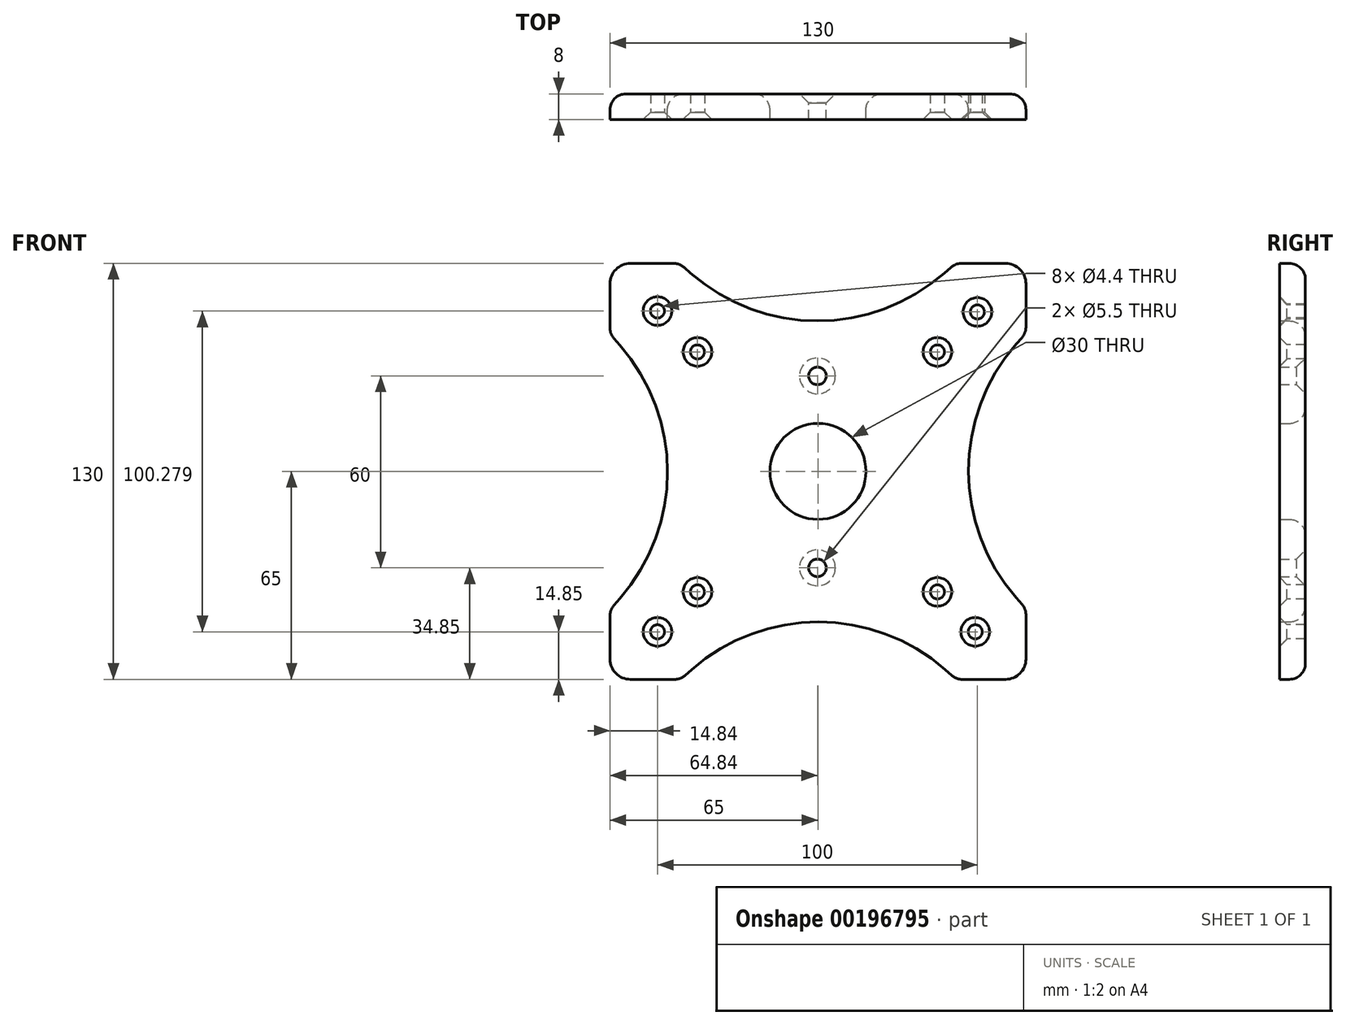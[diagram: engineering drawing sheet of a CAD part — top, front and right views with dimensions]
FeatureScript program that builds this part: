
annotation { "Feature Type Name" : "Feature", "Feature Type Description" : "" }
export const myFeature = defineFeature(function(context is Context, id is Id, definition is map)
    precondition{}
    {
        {
            var Q0;
            Q0=qCreatedBy(makeId("Front.planeOp"),FACE);
            var sketch = newSketch(context, id + "F0", { "sketchPlane" : qUnion([Q0])});
            skLineSegment(sketch, "E0.bottom", {"start": v(-58.49, 65.15) * mm, "end": v(-44.96, 65.15) * mm});
            skLineSegment(sketch, "E0.top", {"start": v(-58.49, -64.85) * mm, "end": v(-44.65, -64.85) * mm});
            skLineSegment(sketch, "E0.left", {"start": v(-64.84, 58.8) * mm, "end": v(-64.84, 44.96) * mm});
            skLineSegment(sketch, "E0.right", {"start": v(65.16, 58.8) * mm, "end": v(65.16, 45.27) * mm});
            skPoint(sketch, "E1.orphan", {"position": v(0, -0.9) * mm});
            skPoint(sketch, "E2.visualSharp", {"position": v(-64.84, 65.15) * mm});
            skArc(sketch, "E2.filletArc", {"start": v(-58.49, 65.15) * mm, "mid": v(-62.98, 63.3) * mm, "end": v(-64.84, 58.8) * mm});
            skPoint(sketch, "E3.visualSharp", {"position": v(65.16, 65.15) * mm});
            skArc(sketch, "E3.filletArc", {"start": v(65.16, 58.8) * mm, "mid": v(63.3, 63.3) * mm, "end": v(58.81, 65.15) * mm});
            skPoint(sketch, "E4.visualSharp", {"position": v(65.16, -64.85) * mm});
            skArc(sketch, "E4.filletArc", {"start": v(58.81, -64.85) * mm, "mid": v(63.3, -62.99) * mm, "end": v(65.16, -58.5) * mm});
            skPoint(sketch, "E5.visualSharp", {"position": v(-64.84, -64.85) * mm});
            skArc(sketch, "E5.filletArc", {"start": v(-64.84, -58.5) * mm, "mid": v(-62.98, -62.99) * mm, "end": v(-58.49, -64.85) * mm});
            skPoint(sketch, "E6", {"position": v(-106.96, 0) * mm});
            skArc(sketch, "E7", {"start": v(-61.82, -39.65) * mm, "mid": v(-46.88, 0) * mm, "end": v(-61.82, 39.65) * mm});
            skLineSegment(sketch, "E8.trimOffspring", {"start": v(-64.84, -44.96) * mm, "end": v(-64.84, -58.5) * mm});
            skLineSegment(sketch, "E9", {"start": v(-61.82, 39.65) * mm, "end": v(-63.6, 41.66) * mm});
            skLineSegment(sketch, "E10", {"start": v(-106.96, 0) * mm, "end": v(0, 0) * mm, "construction": true});
            skLineSegment(sketch, "E11.MirrorCS", {"start": v(-61.82, -39.65) * mm, "end": v(-63.6, -41.66) * mm});
            skLineSegment(sketch, "E12.1.0", {"start": v(39.96, -61.83) * mm, "end": v(41.98, -63.6) * mm});
            skArc(sketch, "E12.1.1", {"start": v(39.96, -61.83) * mm, "mid": v(0.31, -46.9) * mm, "end": v(-39.34, -61.83) * mm});
            skLineSegment(sketch, "E12.1.2", {"start": v(-39.34, -61.83) * mm, "end": v(-41.35, -63.6) * mm});
            skLineSegment(sketch, "E12.2.0", {"start": v(62.14, 39.95) * mm, "end": v(63.92, 41.97) * mm});
            skArc(sketch, "E12.2.1", {"start": v(62.14, 39.95) * mm, "mid": v(47.2, 0.3) * mm, "end": v(62.14, -39.35) * mm});
            skLineSegment(sketch, "E12.2.2", {"start": v(62.14, -39.35) * mm, "end": v(63.92, -41.36) * mm});
            skLineSegment(sketch, "E12.3.0", {"start": v(-39.64, 62.13) * mm, "end": v(-41.66, 63.9) * mm});
            skArc(sketch, "E12.3.1", {"start": v(-39.64, 62.13) * mm, "mid": v(0, 47.2) * mm, "end": v(39.66, 62.13) * mm});
            skLineSegment(sketch, "E12.3.2", {"start": v(39.66, 62.13) * mm, "end": v(41.67, 63.9) * mm});
            skPoint(sketch, "E12.center", {"position": v(0.16, 0.15) * mm});
            skLineSegment(sketch, "E13.trimOffspring", {"start": v(44.97, 65.15) * mm, "end": v(58.81, 65.15) * mm});
            skLineSegment(sketch, "E14.trimOffspring", {"start": v(65.16, -44.66) * mm, "end": v(65.16, -58.5) * mm});
            skLineSegment(sketch, "E15.trimOffspring", {"start": v(45.28, -64.85) * mm, "end": v(58.81, -64.85) * mm});
            skPoint(sketch, "E16.visualSharp", {"position": v(-64.84, 43.08) * mm});
            skArc(sketch, "E16.filletArc", {"start": v(-64.84, 44.96) * mm, "mid": v(-64.52, 43.2) * mm, "end": v(-63.6, 41.66) * mm});
            skPoint(sketch, "E17.visualSharp", {"position": v(-43.07, 65.15) * mm});
            skArc(sketch, "E17.filletArc", {"start": v(-41.66, 63.9) * mm, "mid": v(-43.2, 64.83) * mm, "end": v(-44.96, 65.15) * mm});
            skPoint(sketch, "E18.visualSharp", {"position": v(43.1, 65.15) * mm});
            skArc(sketch, "E18.filletArc", {"start": v(44.97, 65.15) * mm, "mid": v(43.21, 64.83) * mm, "end": v(41.67, 63.9) * mm});
            skPoint(sketch, "E19.visualSharp", {"position": v(65.16, 43.38) * mm});
            skArc(sketch, "E19.filletArc", {"start": v(63.92, 41.97) * mm, "mid": v(64.84, 43.5) * mm, "end": v(65.16, 45.27) * mm});
            skPoint(sketch, "E20.visualSharp", {"position": v(65.16, -42.78) * mm});
            skArc(sketch, "E20.filletArc", {"start": v(65.16, -44.66) * mm, "mid": v(64.84, -42.9) * mm, "end": v(63.92, -41.36) * mm});
            skPoint(sketch, "E21.visualSharp", {"position": v(43.4, -64.85) * mm});
            skArc(sketch, "E21.filletArc", {"start": v(41.98, -63.6) * mm, "mid": v(43.51, -64.53) * mm, "end": v(45.28, -64.85) * mm});
            skPoint(sketch, "E22.visualSharp", {"position": v(-42.77, -64.85) * mm});
            skArc(sketch, "E22.filletArc", {"start": v(-44.65, -64.85) * mm, "mid": v(-42.9, -64.53) * mm, "end": v(-41.35, -63.6) * mm});
            skPoint(sketch, "E23.visualSharp", {"position": v(-64.84, -43.08) * mm});
            skArc(sketch, "E23.filletArc", {"start": v(-63.6, -41.66) * mm, "mid": v(-64.52, -43.2) * mm, "end": v(-64.84, -44.96) * mm});
            skCircle(sketch, "E24", {"center": v(0.16, 0.15) * mm, "radius": 15 * mm});
            skSolve(sketch);
        }
        {
            var Q0;
            Q0=qSketchRegion(id+"F0",true);
            extrude(context, id + "F1", {"entities" : qUnion([Q0]), "depth" : 8 * mm});
        }
        {
            var Q0;
            Q0=makeQuery(id+"F1.opExtrude","CAP_FACE",FACE,{"disambiguationData":[OSD([sQuery(id+"F0.wireOp",EDGE,"E0.bottom"),sQuery(id+"F0.wireOp",EDGE,"E0.top"),sQuery(id+"F0.wireOp",EDGE,"E0.left"),sQuery(id+"F0.wireOp",EDGE,"E0.right"),sQuery(id+"F0.wireOp",EDGE,"E2.filletArc"),sQuery(id+"F0.wireOp",EDGE,"E3.filletArc"),sQuery(id+"F0.wireOp",EDGE,"E4.filletArc"),sQuery(id+"F0.wireOp",EDGE,"E5.filletArc")])],"isStart":false});
            var sketch = newSketch(context, id + "F2", { "sketchPlane" : qUnion([Q0])});
            skPoint(sketch, "E25", {"position": v(50, 50) * mm});
            skPoint(sketch, "E26", {"position": v(-50, 50.28) * mm});
            skPoint(sketch, "E27", {"position": v(-50, -50) * mm});
            skPoint(sketch, "E28", {"position": v(49.32, -50) * mm});
            skPoint(sketch, "E29", {"position": v(-37.5, 37.5) * mm});
            skPoint(sketch, "E30", {"position": v(-37.5, -37.5) * mm});
            skPoint(sketch, "E31", {"position": v(37.5, 37.5) * mm});
            skPoint(sketch, "E32", {"position": v(37.5, -37.5) * mm});
            skSolve(sketch);
        }
        {
            var Q0;
            Q0=sQuery(id+"F2.wireOp",VERTEX,"E26");
            var Q1;
            Q1=sQuery(id+"F2.wireOp",VERTEX,"E25");
            var Q2;
            Q2=sQuery(id+"F2.wireOp",VERTEX,"E28");
            var Q3;
            Q3=sQuery(id+"F2.wireOp",VERTEX,"E27");
            var Q4;
            Q4=sQuery(id+"F2.wireOp",VERTEX,"E29");
            var Q5;
            Q5=sQuery(id+"F2.wireOp",VERTEX,"E31");
            var Q6;
            Q6=sQuery(id+"F2.wireOp",VERTEX,"E32");
            var Q7;
            Q7=sQuery(id+"F2.wireOp",VERTEX,"E30");
            var Q8;
            Q8=makeQuery(id+"F1.opExtrude","SWEPT_BODY",BODY,{"disambiguationData":[OSD([sQuery(id+"F0.wireOp",EDGE,"E0.bottom"),sQuery(id+"F0.wireOp",EDGE,"E0.top"),sQuery(id+"F0.wireOp",EDGE,"E0.left"),sQuery(id+"F0.wireOp",EDGE,"E0.right"),sQuery(id+"F0.wireOp",EDGE,"E2.filletArc"),sQuery(id+"F0.wireOp",EDGE,"E3.filletArc"),sQuery(id+"F0.wireOp",EDGE,"E4.filletArc"),sQuery(id+"F0.wireOp",EDGE,"E5.filletArc")])]});
            hole(context, id + "F3", {"style" : HoleStyle.C_SINK, "endStyle" : HoleEndStyle.THROUGH, "standardTappedOrClearance" : lookupTablePath({ "standard" : "ISO", "fit" : "Normal", "size" : "M4", "type" : "Clearance" }), "standardBlindInLast" : lookupTablePath({ "fit" : "Standard", "standard" : "ISO", "size" : "M4", "type" : "Clearance" }), "holeDiameter" : 4.4 * mm, "cSinkDiameter" : 8.96 * mm, "cSinkAngle" : 90 * degree, "locations" : qUnion([Q0, Q1, Q2, Q3, Q4, Q5, Q6, Q7]), "scope" : qUnion([Q8]), "isTappedThrough" : true});
        }
        {
            var Q0;
            Q0=makeQuery(id+"F1.opExtrude","CAP_FACE",FACE,{"disambiguationData":[OSD([sQuery(id+"F0.wireOp",EDGE,"E0.bottom"),sQuery(id+"F0.wireOp",EDGE,"E0.top"),sQuery(id+"F0.wireOp",EDGE,"E0.left"),sQuery(id+"F0.wireOp",EDGE,"E0.right"),sQuery(id+"F0.wireOp",EDGE,"E2.filletArc"),sQuery(id+"F0.wireOp",EDGE,"E3.filletArc"),sQuery(id+"F0.wireOp",EDGE,"E4.filletArc"),sQuery(id+"F0.wireOp",EDGE,"E5.filletArc")])],"isStart":true});
            var sketch = newSketch(context, id + "F4", { "sketchPlane" : qUnion([Q0])});
            skPoint(sketch, "E33", {"position": v(0, 30) * mm});
            skPoint(sketch, "E34", {"position": v(0, -30) * mm});
            skSolve(sketch);
        }
        {
            var Q0;
            Q0=sQuery(id+"F4.wireOp",VERTEX,"E34");
            var Q1;
            Q1=sQuery(id+"F4.wireOp",VERTEX,"E33");
            var Q2;
            Q2=makeQuery(id+"F1.opExtrude","SWEPT_BODY",BODY,{"disambiguationData":[OSD([sQuery(id+"F0.wireOp",EDGE,"E0.bottom"),sQuery(id+"F0.wireOp",EDGE,"E0.top"),sQuery(id+"F0.wireOp",EDGE,"E0.left"),sQuery(id+"F0.wireOp",EDGE,"E0.right"),sQuery(id+"F0.wireOp",EDGE,"E2.filletArc"),sQuery(id+"F0.wireOp",EDGE,"E3.filletArc"),sQuery(id+"F0.wireOp",EDGE,"E4.filletArc"),sQuery(id+"F0.wireOp",EDGE,"E5.filletArc")])]});
            hole(context, id + "F5", {"style" : HoleStyle.C_SINK, "endStyle" : HoleEndStyle.THROUGH, "standardTappedOrClearance" : lookupTablePath({ "standard" : "ISO", "fit" : "Normal", "size" : "M5", "type" : "Clearance" }), "standardBlindInLast" : lookupTablePath({ "fit" : "Standard", "standard" : "ISO", "size" : "M5", "type" : "Clearance" }), "holeDiameter" : 5.5 * mm, "cSinkDiameter" : 11.2 * mm, "cSinkAngle" : 90 * degree, "locations" : qUnion([Q0, Q1]), "scope" : qUnion([Q2]), "isTappedThrough" : true});
        }
        {
            var Q0;
            Q0=makeQuery(id+"F1.opExtrude","CAP_EDGE",EDGE,{"disambiguationData":[OSD([sQuery(id+"F0.wireOp",EDGE,"E0.top")])],"isStart":true});
            var Q1;
            Q1=makeQuery(id+"F1.opExtrude","CAP_EDGE",EDGE,{"disambiguationData":[OSD([sQuery(id+"F0.wireOp",EDGE,"E4.filletArc")])],"isStart":true});
            var Q2;
            Q2=makeQuery(id+"F1.opExtrude","CAP_EDGE",EDGE,{"disambiguationData":[OSD([sQuery(id+"F0.wireOp",EDGE,"E0.right")])],"isStart":true});
            var Q3;
            Q3=makeQuery(id+"F1.opExtrude","CAP_EDGE",EDGE,{"disambiguationData":[OSD([sQuery(id+"F0.wireOp",EDGE,"E5.filletArc")])],"isStart":true});
            var Q4;
            Q4=makeQuery(id+"F1.opExtrude","CAP_EDGE",EDGE,{"disambiguationData":[OSD([sQuery(id+"F0.wireOp",EDGE,"E0.left")])],"isStart":true});
            var Q5;
            Q5=makeQuery(id+"F1.opExtrude","CAP_EDGE",EDGE,{"disambiguationData":[OSD([sQuery(id+"F0.wireOp",EDGE,"E2.filletArc")])],"isStart":true});
            var Q6;
            Q6=makeQuery(id+"F1.opExtrude","CAP_EDGE",EDGE,{"disambiguationData":[OSD([sQuery(id+"F0.wireOp",EDGE,"E0.bottom")])],"isStart":true});
            var Q7;
            Q7=makeQuery(id+"F1.opExtrude","CAP_EDGE",EDGE,{"disambiguationData":[OSD([sQuery(id+"F0.wireOp",EDGE,"E3.filletArc")])],"isStart":true});
            var Q8;
            Q8=makeQuery(id+"F1.opExtrude","CAP_EDGE",EDGE,{"disambiguationData":[OSD([sQuery(id+"F0.wireOp",EDGE,"E24")])],"isStart":true});
            fillet(context, id + "F6", {"entities" : qUnion([Q0, Q1, Q2, Q3, Q4, Q5, Q6, Q7, Q8]), "radius" : 5 * mm, "tangentPropagation" : true, "allowEdgeOverflow" : false});
        }
    });
